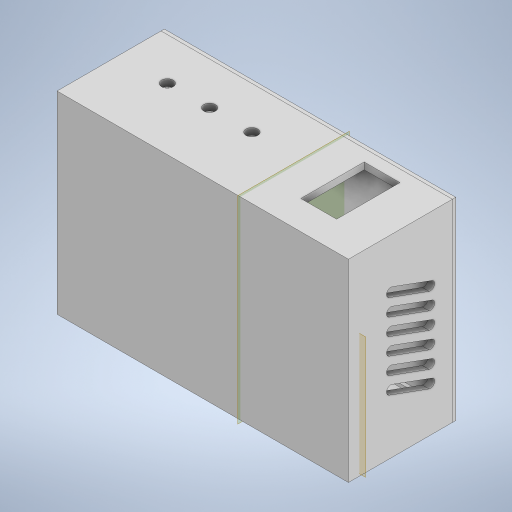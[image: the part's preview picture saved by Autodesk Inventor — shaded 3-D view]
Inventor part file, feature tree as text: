
AUTODESK INVENTOR PART (.ipt)
format: ipt  version: 2024 (Build 280153000, 153)  size: 498,176 bytes
history: native  units: mm
features: sketch x11, extrude x9, projected_geometry x6, reference x5, other x3, plane x2, hole x2, chamfer x1
ambient origin geometry x8: Origin, YZ Plane, XZ Plane, XY Plane, X Axis, Y Axis, Z Axis, Center Point
bodies: Solid1 (feature_tree)
feature tree (39):
  plane  "Work Plane1"
  extrude  "Extrusion1"  Depth=2.7mm
  extrude  "Extrusion2"  Depth=8.0mm
  extrude  "Extrusion3"  Depth=8.0mm
  extrude  "Extrusion4"  Depth=1.5mm TaperAngle=0.0deg
  extrude  "Extrusion5"  Depth=60.0mm TaperAngle=0.0deg
  extrude  "Extrusion6"  Depth=4.0mm
  plane  "Work Plane2"
  extrude  "Extrusion11"  Depth=21.2mm
  chamfer  "Chamfer1"  Distance=60.0mm
  hole  "Hole1"  [1 undecoded]
  extrude  "Extrusion12"  Depth=2.0mm
  extrude  "Extrusion13"  Depth=2.0mm
  hole  "Hole2"  [1 undecoded]
  sketch  "Sketch1"  dims[d0=2.7mm d1=2.7mm]
  reference  "Reference1"
  sketch  "Sketch2"  dims[d2=2.7mm d3=8.0mm]
  reference  "Reference2"
  sketch  "Sketch3"  dims[d4=8.0mm d5=8.0mm]
  projected_geometry  "Projected Loop1"
  sketch  "Sketch4"  dims[d6=5.0mm d7=0.0mm d8=1.5mm d9=0.0mm]
  projected_geometry  "Projected Loop2"
  sketch  "Sketch5"  dims[d10=0.5mm d13=60.0mm d14=0.0mm]
  reference  "Reference3"
  reference  "Reference4"
  reference  "Reference5"
  sketch  "Sketch6"  dims[d15=40.0mm d16=4.0mm]
  projected_geometry  "Projected Loop3"
  sketch  "Sketch11"  dims[d17=37.5mm d18=21.2mm]
  projected_geometry  "Projected Loop9"
  sketch  "Sketch12"  dims[d19=6.85mm]
  sketch  "Sketch13"  dims[d20=30.0mm d22=25.0mm d23=10.0mm d25=10.0mm]
  projected_geometry  "Projected Loop10"
  other  "pokrywka"
  sketch  "Sketch14"  dims[d27=7.0mm]
  projected_geometry  "Projected Loop11"
  sketch  "Sketch15"  dims[d28=20.0mm d29=60.0mm d30=0.0mm d31=25.0mm d32=8.0mm d33=12.7mm d34=12.7mm d35=12.7mm d36=30.2mm d37=60.0mm d38=0.0mm d39=25.0mm d40=3.490659mm d41=5.0mm d42=60.0mm d44=10.0mm d45=10.0mm d47=10.0mm d49=0.0mm d50=0.0mm d51=60.0mm d77=10.0mm d78=10.0mm d79=10.0mm d80=10.0mm d81=10.0mm d82=0.0mm d83=5.0mm d84=2.0mm d85=45.0deg d86=2.7mm d87=6.0mm d88=4.0mm d89=2.0mm d90=90.0deg d91=8.0mm d92=20.594885mm d93=0.5mm d94=2.0mm d95=2.0mm d96=0.0mm d97=2.0mm d98=0.0mm d99=3.2mm d100=6.0mm d101=5.6mm d102=2.0mm d103=90.0deg d104=8.0mm d105=20.594885mm]
  parser-record x1  (decoder bookkeeping rows leaked as tree rows — omitted from the tree; the rows remain in map.json)
  other  "homemade_attocube.iam"
note: 2 required parameter values undecoded (feature->parameter linkage not recoverable at this tier; creation-order binding heuristic only, values carry confidence <= 0.55)
note: 1 file-system path scrubbed to <path> (originals preserved in map.json)
